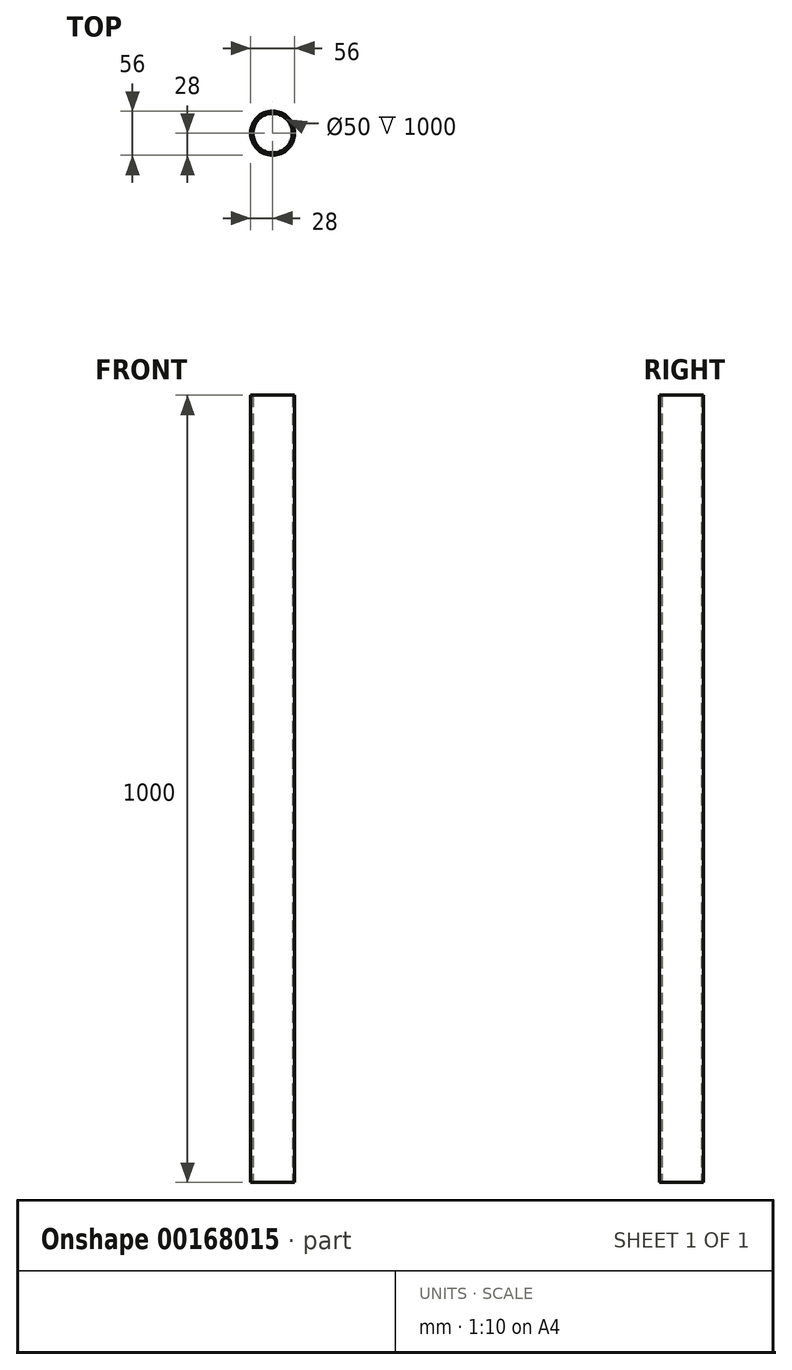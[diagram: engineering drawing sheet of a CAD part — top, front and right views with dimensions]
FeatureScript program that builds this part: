
annotation { "Feature Type Name" : "Feature", "Feature Type Description" : "" }
export const myFeature = defineFeature(function(context is Context, id is Id, definition is map)
    precondition{}
    {
        {
            var Q0;
            Q0=qCreatedBy(makeId("Top.planeOp"),FACE);
            var sketch = newSketch(context, id + "F0", { "sketchPlane" : qUnion([Q0])});
            skCircle(sketch, "E0", {"center": v(0, 0) * mm, "radius": 25 * mm});
            skCircle(sketch, "E1.0", {"center": v(0, 0) * mm, "radius": 28 * mm});
            skSolve(sketch);
        }
        {
            var Q0;
            Q0 = qSketchRegion(id + "F0", true);
            extrude(context, id + "F1", {"entities" : qUnion([Q0]), "depth" : 1000 * mm, "offsetDistance" : 25 * mm, "symmetric" : true});
        }
    });
